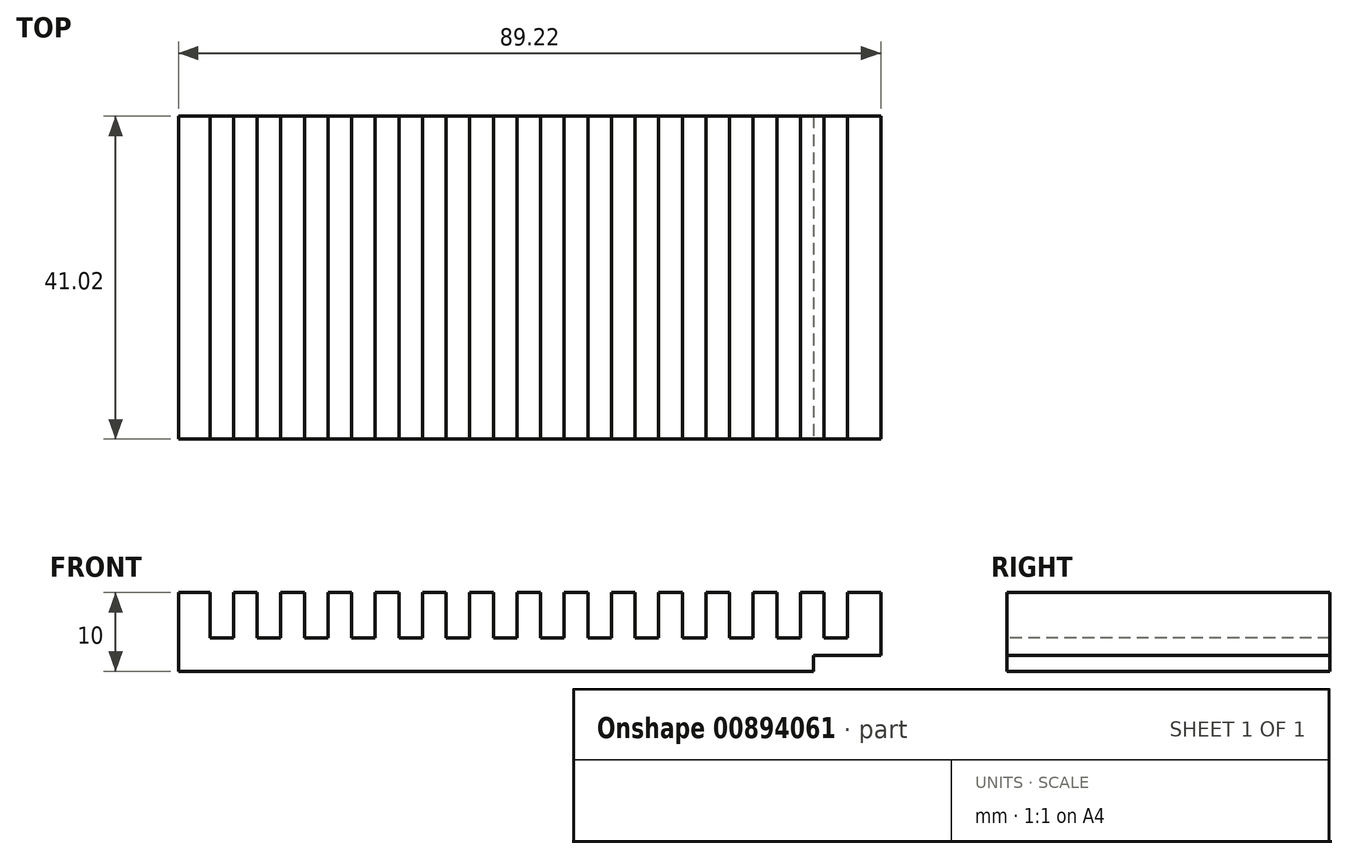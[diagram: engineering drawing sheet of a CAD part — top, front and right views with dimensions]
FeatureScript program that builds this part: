
annotation { "Feature Type Name" : "Feature", "Feature Type Description" : "" }
export const myFeature = defineFeature(function(context is Context, id is Id, definition is map)
    precondition{}
    {
        {
            var Q0;
            Q0=qCreatedBy(makeId("Top.planeOp"),FACE);
            var sketch = newSketch(context, id + "F0", { "sketchPlane" : qUnion([Q0])});
            skLineSegment(sketch, "E0.bottom", {"start": v(-30.4, 18.8) * mm, "end": v(58.82, 18.8) * mm});
            skLineSegment(sketch, "E0.top", {"start": v(-30.4, -22.22) * mm, "end": v(58.82, -22.22) * mm});
            skLineSegment(sketch, "E0.left", {"start": v(-30.4, 18.8) * mm, "end": v(-30.4, -22.22) * mm});
            skLineSegment(sketch, "E0.right", {"start": v(58.82, 18.8) * mm, "end": v(58.82, -22.22) * mm});
            skSolve(sketch);
        }
        {
            var Q0;
            Q0 = qSketchRegion(id + "F0", true);
            extrude(context, id + "F1", {"entities" : qUnion([Q0]), "depth" : 10 * mm, "offsetDistance" : 25 * mm});
        }
        {
            var Q0;
            Q0=makeQuery(id+"F1.opExtrude","SWEPT_FACE",FACE,{"disambiguationData":[OSD([sQuery(id+"F0.wireOp",EDGE,"E0.top")])]});
            var sketch = newSketch(context, id + "F2", { "sketchPlane" : qUnion([Q0])});
            skLineSegment(sketch, "E1.bottom", {"start": v(50.24, 0) * mm, "end": v(58.82, 0) * mm});
            skLineSegment(sketch, "E1.top", {"start": v(50.24, 2) * mm, "end": v(58.82, 2) * mm});
            skLineSegment(sketch, "E1.left", {"start": v(50.24, 0) * mm, "end": v(50.24, 2) * mm});
            skLineSegment(sketch, "E1.right", {"start": v(58.82, 0) * mm, "end": v(58.82, 2) * mm});
            skSolve(sketch);
        }
        {
            var Q0;
            Q0 = qSketchRegion(id + "F2", true);
            extrude(context, id + "F3", {"entities" : qUnion([Q0]), "operationType" : NewBodyOperationType.REMOVE, "endBound" : BoundingType.THROUGH_ALL, "oppositeDirection" : true, "depth" : 25 * mm, "offsetDistance" : 25 * mm});
        }
        {
            var Q0;
            Q0=makeQuery(id+"F1.opExtrude","SWEPT_FACE",FACE,{"disambiguationData":[OSD([sQuery(id+"F0.wireOp",EDGE,"E0.top")])]});
            var sketch = newSketch(context, id + "F4", { "sketchPlane" : qUnion([Q0])});
            skLineSegment(sketch, "E2.bottom", {"start": v(-30.4, 10) * mm, "end": v(-26.4, 10) * mm, "construction": true});
            skLineSegment(sketch, "E2.top", {"start": v(-30.4, 4.25) * mm, "end": v(-26.4, 4.25) * mm, "construction": true});
            skLineSegment(sketch, "E2.left", {"start": v(-30.4, 10) * mm, "end": v(-30.4, 4.25) * mm, "construction": true});
            skLineSegment(sketch, "E2.right", {"start": v(-26.4, 10) * mm, "end": v(-26.4, 4.25) * mm});
            skLineSegment(sketch, "E3.bottom", {"start": v(-26.4, 4.25) * mm, "end": v(-23.4, 4.25) * mm});
            skLineSegment(sketch, "E3.top", {"start": v(-26.4, 10) * mm, "end": v(-23.4, 10) * mm});
            skLineSegment(sketch, "E3.left", {"start": v(-26.4, 4.25) * mm, "end": v(-26.4, 10) * mm});
            skLineSegment(sketch, "E3.right", {"start": v(-23.4, 4.25) * mm, "end": v(-23.4, 10) * mm});
            skLineSegment(sketch, "E4.1.0.0", {"start": v(-20.4, 10) * mm, "end": v(-17.4, 10) * mm});
            skLineSegment(sketch, "E4.1.0.1", {"start": v(-17.4, 4.25) * mm, "end": v(-17.4, 10) * mm});
            skLineSegment(sketch, "E4.1.0.2", {"start": v(-20.4, 4.25) * mm, "end": v(-20.4, 10) * mm});
            skLineSegment(sketch, "E4.1.0.3", {"start": v(-20.4, 4.25) * mm, "end": v(-17.4, 4.25) * mm});
            skLineSegment(sketch, "E4.2.0.0", {"start": v(-14.4, 10) * mm, "end": v(-11.4, 10) * mm});
            skLineSegment(sketch, "E4.2.0.1", {"start": v(-11.4, 4.25) * mm, "end": v(-11.4, 10) * mm});
            skLineSegment(sketch, "E4.2.0.2", {"start": v(-14.4, 4.25) * mm, "end": v(-14.4, 10) * mm});
            skLineSegment(sketch, "E4.2.0.3", {"start": v(-14.4, 4.25) * mm, "end": v(-11.4, 4.25) * mm});
            skLineSegment(sketch, "E4.3.0.0", {"start": v(-8.4, 10) * mm, "end": v(-5.4, 10) * mm});
            skLineSegment(sketch, "E4.3.0.1", {"start": v(-5.4, 4.25) * mm, "end": v(-5.4, 10) * mm});
            skLineSegment(sketch, "E4.3.0.2", {"start": v(-8.4, 4.25) * mm, "end": v(-8.4, 10) * mm});
            skLineSegment(sketch, "E4.3.0.3", {"start": v(-8.4, 4.25) * mm, "end": v(-5.4, 4.25) * mm});
            skLineSegment(sketch, "E4.4.0.0", {"start": v(-2.4, 10) * mm, "end": v(0.6, 10) * mm});
            skLineSegment(sketch, "E4.4.0.1", {"start": v(0.6, 4.25) * mm, "end": v(0.6, 10) * mm});
            skLineSegment(sketch, "E4.4.0.2", {"start": v(-2.4, 4.25) * mm, "end": v(-2.4, 10) * mm});
            skLineSegment(sketch, "E4.4.0.3", {"start": v(-2.4, 4.25) * mm, "end": v(0.6, 4.25) * mm});
            skLineSegment(sketch, "E4.5.0.0", {"start": v(3.6, 10) * mm, "end": v(6.6, 10) * mm});
            skLineSegment(sketch, "E4.5.0.1", {"start": v(6.6, 4.25) * mm, "end": v(6.6, 10) * mm});
            skLineSegment(sketch, "E4.5.0.2", {"start": v(3.6, 4.25) * mm, "end": v(3.6, 10) * mm});
            skLineSegment(sketch, "E4.5.0.3", {"start": v(3.6, 4.25) * mm, "end": v(6.6, 4.25) * mm});
            skLineSegment(sketch, "E4.6.0.0", {"start": v(9.6, 10) * mm, "end": v(12.6, 10) * mm});
            skLineSegment(sketch, "E4.6.0.1", {"start": v(12.6, 4.25) * mm, "end": v(12.6, 10) * mm});
            skLineSegment(sketch, "E4.6.0.2", {"start": v(9.6, 4.25) * mm, "end": v(9.6, 10) * mm});
            skLineSegment(sketch, "E4.6.0.3", {"start": v(9.6, 4.25) * mm, "end": v(12.6, 4.25) * mm});
            skLineSegment(sketch, "E4.7.0.0", {"start": v(15.6, 10) * mm, "end": v(18.6, 10) * mm});
            skLineSegment(sketch, "E4.7.0.1", {"start": v(18.6, 4.25) * mm, "end": v(18.6, 10) * mm});
            skLineSegment(sketch, "E4.7.0.2", {"start": v(15.6, 4.25) * mm, "end": v(15.6, 10) * mm});
            skLineSegment(sketch, "E4.7.0.3", {"start": v(15.6, 4.25) * mm, "end": v(18.6, 4.25) * mm});
            skLineSegment(sketch, "E4.8.0.0", {"start": v(21.6, 10) * mm, "end": v(24.6, 10) * mm});
            skLineSegment(sketch, "E4.8.0.1", {"start": v(24.6, 4.25) * mm, "end": v(24.6, 10) * mm});
            skLineSegment(sketch, "E4.8.0.2", {"start": v(21.6, 4.25) * mm, "end": v(21.6, 10) * mm});
            skLineSegment(sketch, "E4.8.0.3", {"start": v(21.6, 4.25) * mm, "end": v(24.6, 4.25) * mm});
            skLineSegment(sketch, "E4.9.0.0", {"start": v(27.6, 10) * mm, "end": v(30.6, 10) * mm});
            skLineSegment(sketch, "E4.9.0.1", {"start": v(30.6, 4.25) * mm, "end": v(30.6, 10) * mm});
            skLineSegment(sketch, "E4.9.0.2", {"start": v(27.6, 4.25) * mm, "end": v(27.6, 10) * mm});
            skLineSegment(sketch, "E4.9.0.3", {"start": v(27.6, 4.25) * mm, "end": v(30.6, 4.25) * mm});
            skLineSegment(sketch, "E4.10.0.0", {"start": v(33.6, 10) * mm, "end": v(36.6, 10) * mm});
            skLineSegment(sketch, "E4.10.0.1", {"start": v(36.6, 4.25) * mm, "end": v(36.6, 10) * mm});
            skLineSegment(sketch, "E4.10.0.2", {"start": v(33.6, 4.25) * mm, "end": v(33.6, 10) * mm});
            skLineSegment(sketch, "E4.10.0.3", {"start": v(33.6, 4.25) * mm, "end": v(36.6, 4.25) * mm});
            skLineSegment(sketch, "E4.11.0.0", {"start": v(39.6, 10) * mm, "end": v(42.6, 10) * mm});
            skLineSegment(sketch, "E4.11.0.1", {"start": v(42.6, 4.25) * mm, "end": v(42.6, 10) * mm});
            skLineSegment(sketch, "E4.11.0.2", {"start": v(39.6, 4.25) * mm, "end": v(39.6, 10) * mm});
            skLineSegment(sketch, "E4.11.0.3", {"start": v(39.6, 4.25) * mm, "end": v(42.6, 4.25) * mm});
            skLineSegment(sketch, "E4.12.0.0", {"start": v(45.6, 10) * mm, "end": v(48.6, 10) * mm});
            skLineSegment(sketch, "E4.12.0.1", {"start": v(48.6, 4.25) * mm, "end": v(48.6, 10) * mm});
            skLineSegment(sketch, "E4.12.0.2", {"start": v(45.6, 4.25) * mm, "end": v(45.6, 10) * mm});
            skLineSegment(sketch, "E4.12.0.3", {"start": v(45.6, 4.25) * mm, "end": v(48.6, 4.25) * mm});
            skLineSegment(sketch, "E4.13.0.0", {"start": v(51.6, 10) * mm, "end": v(54.6, 10) * mm});
            skLineSegment(sketch, "E4.13.0.1", {"start": v(54.6, 4.25) * mm, "end": v(54.6, 10) * mm});
            skLineSegment(sketch, "E4.13.0.2", {"start": v(51.6, 4.25) * mm, "end": v(51.6, 10) * mm});
            skLineSegment(sketch, "E4.13.0.3", {"start": v(51.6, 4.25) * mm, "end": v(54.6, 4.25) * mm});
            skLineSegment(sketch, "E4.direction1", {"start": v(-26.4, 10) * mm, "end": v(-20.4, 10) * mm, "construction": true});
            skSolve(sketch);
        }
        {
            var Q0;
            Q0 = qSketchRegion(id + "F4", true);
            extrude(context, id + "F5", {"entities" : qUnion([Q0]), "operationType" : NewBodyOperationType.REMOVE, "endBound" : BoundingType.THROUGH_ALL, "oppositeDirection" : true, "depth" : 25 * mm, "offsetDistance" : 25 * mm});
        }
    });
